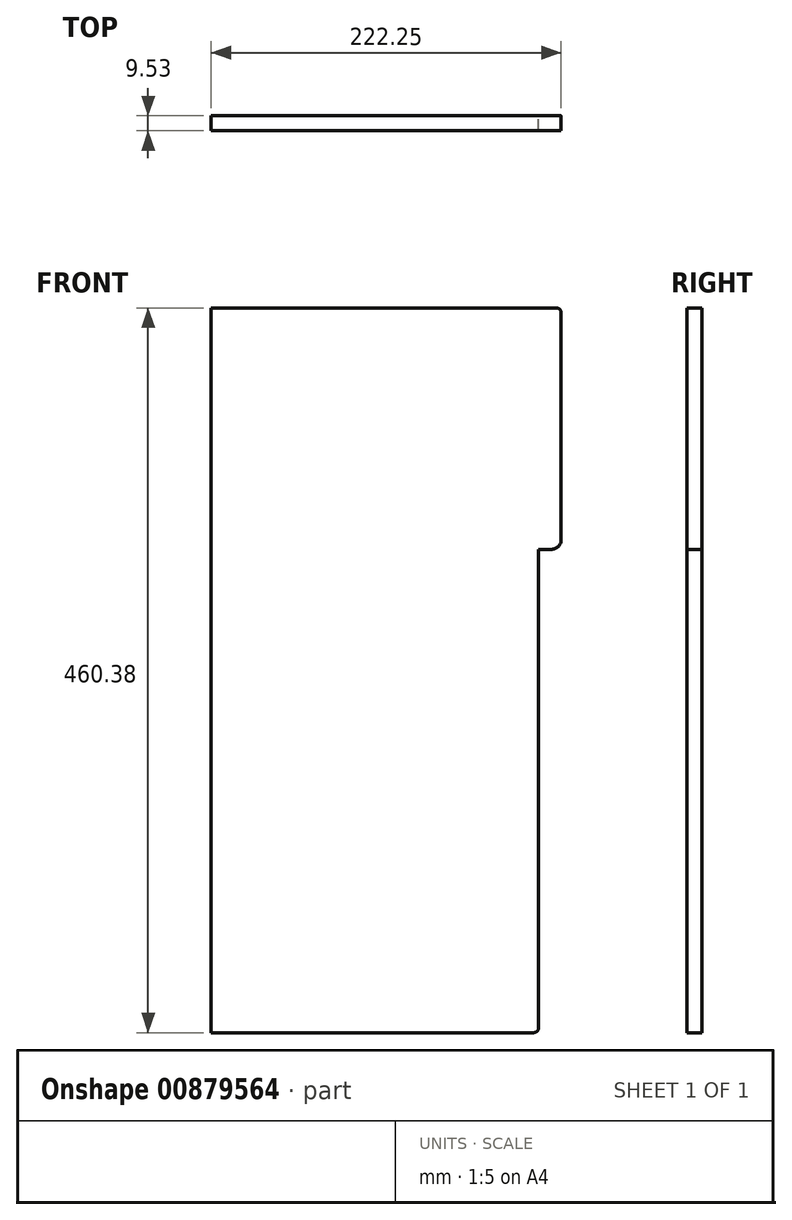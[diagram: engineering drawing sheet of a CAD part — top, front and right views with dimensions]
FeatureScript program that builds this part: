
annotation { "Feature Type Name" : "Feature", "Feature Type Description" : "" }
export const myFeature = defineFeature(function(context is Context, id is Id, definition is map)
    precondition{}
    {
        {
            var Q0;
            Q0=qCreatedBy(makeId("Front.planeOp"),FACE);
            var sketch = newSketch(context, id + "F0", { "sketchPlane" : qUnion([Q0])});
            skLineSegment(sketch, "E0.bottom", {"start": v(103.98, 230.19) * mm, "end": v(-103.98, 230.19) * mm});
            skLineSegment(sketch, "E0.top", {"start": v(103.98, -230.19) * mm, "end": v(-103.98, -230.19) * mm});
            skLineSegment(sketch, "E0.left", {"start": v(103.98, 230.19) * mm, "end": v(103.98, -230.19) * mm});
            skLineSegment(sketch, "E0.right", {"start": v(-103.98, 230.19) * mm, "end": v(-103.98, -230.19) * mm});
            skPoint(sketch, "E0.middle", {"position": v(0, 0) * mm});
            skSolve(sketch);
        }
        {
            var Q0;
            Q0 = qSketchRegion(id + "F0", true);
            extrude(context, id + "F1", {"entities" : qUnion([Q0]), "depth" : 9.52 * mm, "offsetDistance" : 25.4 * mm});
        }
        {
            var Q0;
            Q0=qCreatedBy(makeId("Front.planeOp"),FACE);
            var sketch = newSketch(context, id + "F2", { "sketchPlane" : qUnion([Q0])});
            skLineSegment(sketch, "E1.bottom", {"start": v(103.98, 76.73) * mm, "end": v(118.27, 76.73) * mm});
            skLineSegment(sketch, "E1.top", {"start": v(103.98, 230.19) * mm, "end": v(118.27, 230.19) * mm});
            skLineSegment(sketch, "E1.left", {"start": v(103.98, 76.73) * mm, "end": v(103.98, 230.19) * mm});
            skLineSegment(sketch, "E1.right", {"start": v(118.27, 76.73) * mm, "end": v(118.27, 230.19) * mm});
            skLineSegment(sketch, "E2.0", {"start": v(103.98, 230.19) * mm, "end": v(103.98, -230.19) * mm, "construction": true});
            skSolve(sketch);
        }
        {
            var Q0;
            Q0 = qSketchRegion(id + "F2", true);
            var Q1;
            Q1=makeQuery(id+"F1.opExtrude","CAP_FACE",FACE,{"disambiguationData":[OSD([sQuery(id+"F0.wireOp",EDGE,"E0.bottom"),sQuery(id+"F0.wireOp",EDGE,"E0.top"),sQuery(id+"F0.wireOp",EDGE,"E0.left"),sQuery(id+"F0.wireOp",EDGE,"E0.right")])],"isStart":false});
            extrude(context, id + "F3", {"entities" : qUnion([Q0]), "operationType" : NewBodyOperationType.ADD, "endBound" : BoundingType.UP_TO_SURFACE, "depth" : 25.4 * mm, "endBoundEntityFace" : qUnion([Q1]), "offsetDistance" : 25.4 * mm});
        }
        {
            var Q0;
            Q0=makeQuery(id+"F1.opExtrude","SWEPT_EDGE",EDGE,{"disambiguationData":[OSD([sQuery(id+"F0.wireOp",EDGE,"E0.top"),sQuery(id+"F0.wireOp",EDGE,"E0.left")])]});
            var Q1;
            Q1=makeQuery(id+"F3.opExtrude","SWEPT_EDGE",EDGE,{"disambiguationData":[OSD([sQuery(id+"F2.wireOp",EDGE,"E1.top"),sQuery(id+"F2.wireOp",EDGE,"E1.right")])]});
            fillet(context, id + "F4", {"entities" : qUnion([Q0, Q1]), "radius" : 3.17 * mm, "tangentPropagation" : true, "allowEdgeOverflow" : false});
        }
        {
            var Q0;
            Q0=makeQuery(id+"F3.opExtrude","SWEPT_EDGE",EDGE,{"disambiguationData":[OSD([sQuery(id+"F2.wireOp",EDGE,"E1.bottom"),sQuery(id+"F2.wireOp",EDGE,"E1.left")])]});
            var Q1;
            Q1=makeQuery(id+"F3.opExtrude","SWEPT_EDGE",EDGE,{"disambiguationData":[OSD([sQuery(id+"F2.wireOp",EDGE,"E1.bottom"),sQuery(id+"F2.wireOp",EDGE,"E1.right")])]});
            fillet(context, id + "F5", {"entities" : qUnion([Q0, Q1]), "radius" : 6.35 * mm, "tangentPropagation" : true, "allowEdgeOverflow" : false});
        }
    });
